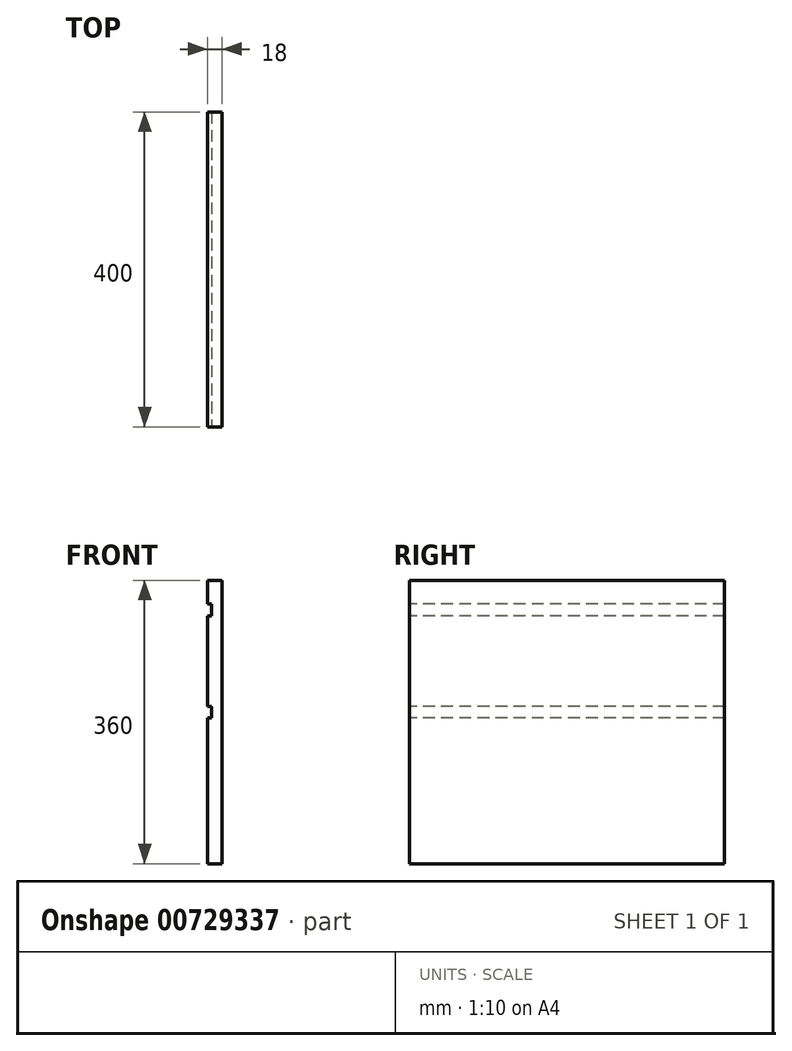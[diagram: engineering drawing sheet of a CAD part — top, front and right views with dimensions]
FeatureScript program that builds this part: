
annotation { "Feature Type Name" : "Feature", "Feature Type Description" : "" }
export const myFeature = defineFeature(function(context is Context, id is Id, definition is map)
    precondition{}
    {
        {
            var Q0;
            Q0=qCreatedBy(makeId("Front.planeOp"),FACE);
            var sketch = newSketch(context, id + "F0", { "sketchPlane" : qUnion([Q0])});
            skLineSegment(sketch, "E0.bottom", {"start": v(0, 0) * mm, "end": v(18, 0) * mm});
            skLineSegment(sketch, "E0.top", {"start": v(0, 360) * mm, "end": v(18, 360) * mm});
            skLineSegment(sketch, "E0.left", {"start": v(0, 0) * mm, "end": v(0, 360) * mm});
            skLineSegment(sketch, "E0.right", {"start": v(18, 0) * mm, "end": v(18, 360) * mm});
            skSolve(sketch);
        }
        {
            var Q0;
            Q0=qSketchRegion(id+"F0",true);
            extrude(context, id + "F1", {"entities" : qUnion([Q0]), "oppositeDirection" : true, "depth" : 400 * mm, "offsetDistance" : 25 * mm});
        }
        {
            var Q0;
            Q0=makeQuery(id+"F1.opExtrude","CAP_FACE",FACE,{"disambiguationData":[OSD([sQuery(id+"F0.wireOp",EDGE,"E0.bottom"),sQuery(id+"F0.wireOp",EDGE,"E0.top"),sQuery(id+"F0.wireOp",EDGE,"E0.left"),sQuery(id+"F0.wireOp",EDGE,"E0.right")])],"isStart":true});
            var sketch = newSketch(context, id + "F2", { "sketchPlane" : qUnion([Q0])});
            skLineSegment(sketch, "E1", {"start": v(9, 360) * mm, "end": v(9, 0) * mm, "construction": true});
            skLineSegment(sketch, "E2.MirrorCS", {"start": v(5, 185) * mm, "end": v(5, 200) * mm});
            skLineSegment(sketch, "E3.MirrorCS", {"start": v(0, 185) * mm, "end": v(0, 200) * mm});
            skLineSegment(sketch, "E4.MirrorCS", {"start": v(0, 200) * mm, "end": v(5, 200) * mm});
            skLineSegment(sketch, "E5.MirrorCS", {"start": v(0, 185) * mm, "end": v(5, 185) * mm});
            skLineSegment(sketch, "E6.MirrorCS", {"start": v(5, 330) * mm, "end": v(5, 315) * mm});
            skLineSegment(sketch, "E7.MirrorCS", {"start": v(0, 315) * mm, "end": v(5, 315) * mm});
            skLineSegment(sketch, "E8.MirrorCS", {"start": v(0, 330) * mm, "end": v(0, 315) * mm});
            skLineSegment(sketch, "E9.MirrorCS", {"start": v(0, 330) * mm, "end": v(5, 330) * mm});
            skSolve(sketch);
        }
        {
            var Q0;
            Q0=qSketchRegion(id+"F2",true);
            var Q1;
            Q1=makeQuery(id+"F1.opExtrude","CAP_FACE",FACE,{"disambiguationData":[OSD([sQuery(id+"F0.wireOp",EDGE,"E0.bottom"),sQuery(id+"F0.wireOp",EDGE,"E0.top"),sQuery(id+"F0.wireOp",EDGE,"E0.left"),sQuery(id+"F0.wireOp",EDGE,"E0.right")])],"isStart":false});
            extrude(context, id + "F3", {"entities" : qUnion([Q0]), "operationType" : NewBodyOperationType.REMOVE, "endBound" : BoundingType.THROUGH_ALL, "oppositeDirection" : true, "depth" : 25 * mm, "endBoundEntityFace" : qUnion([Q1]), "offsetDistance" : 25 * mm});
        }
    });
